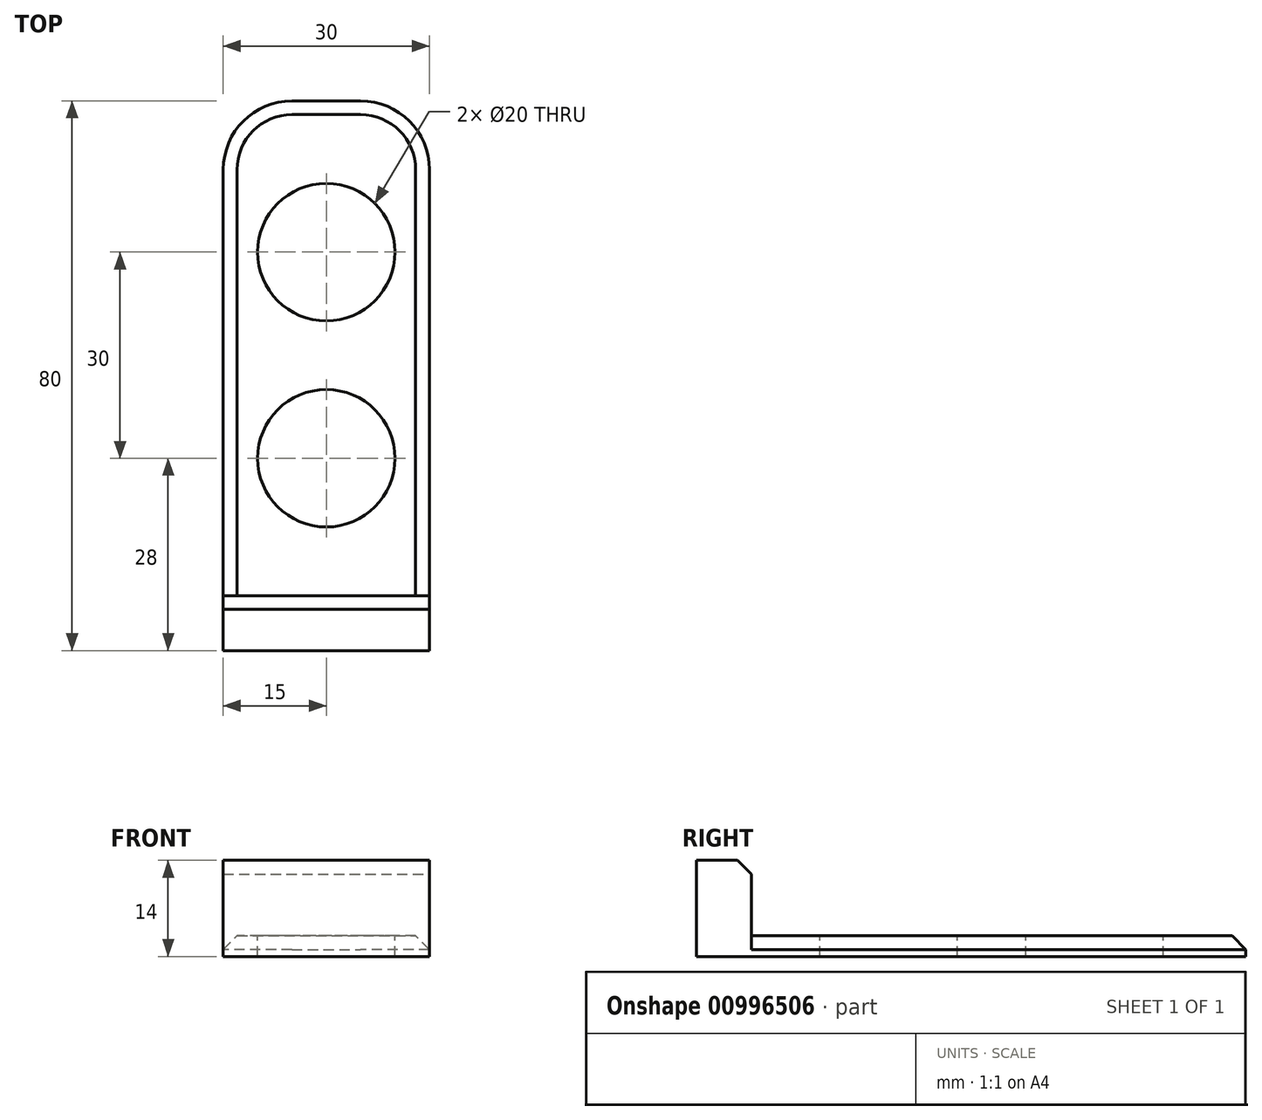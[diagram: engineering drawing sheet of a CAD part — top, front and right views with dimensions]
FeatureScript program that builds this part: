
annotation { "Feature Type Name" : "Feature", "Feature Type Description" : "" }
export const myFeature = defineFeature(function(context is Context, id is Id, definition is map)
    precondition{}
    {
        {
            var Q0;
            Q0=qCreatedBy(makeId("Top.planeOp"),FACE);
            var sketch = newSketch(context, id + "F0", { "sketchPlane" : qUnion([Q0])});
            skLineSegment(sketch, "E0.bottom", {"start": v(15, -40) * mm, "end": v(-15, -40) * mm});
            skLineSegment(sketch, "E0.top", {"start": v(15, 40) * mm, "end": v(-15, 40) * mm});
            skLineSegment(sketch, "E0.left", {"start": v(15, -40) * mm, "end": v(15, 40) * mm});
            skLineSegment(sketch, "E0.right", {"start": v(-15, -40) * mm, "end": v(-15, 40) * mm});
            skPoint(sketch, "E0.middle", {"position": v(0, 0) * mm});
            skSolve(sketch);
        }
        {
            var Q0;
            Q0=makeQuery(id+"F0.imprint","IMPRINT",FACE,{"disambiguationData":[TD([[makeQuery(id+"F0.imprint","IMPRINT",EDGE,{"derivedFrom":sQuery(id+"F0.wireOp",EDGE,"E0.bottom")}),-1.0]])]});
            extrude(context, id + "F1", {"entities" : qUnion([Q0]), "depth" : 3 * mm, "offsetDistance" : 25 * mm});
        }
        {
            var Q0;
            Q0=makeQuery(id+"F1.opExtrude","CAP_FACE",FACE,{"disambiguationData":[OSD([sQuery(id+"F0.wireOp",EDGE,"E0.bottom"),sQuery(id+"F0.wireOp",EDGE,"E0.top"),sQuery(id+"F0.wireOp",EDGE,"E0.left"),sQuery(id+"F0.wireOp",EDGE,"E0.right")])],"isStart":false});
            var sketch = newSketch(context, id + "F2", { "sketchPlane" : qUnion([Q0])});
            skLineSegment(sketch, "E1.bottom", {"start": v(-15, -40) * mm, "end": v(15, -40) * mm});
            skLineSegment(sketch, "E1.top", {"start": v(-15, -32) * mm, "end": v(15, -32) * mm});
            skLineSegment(sketch, "E1.left", {"start": v(-15, -40) * mm, "end": v(-15, -32) * mm});
            skLineSegment(sketch, "E1.right", {"start": v(15, -40) * mm, "end": v(15, -32) * mm});
            skSolve(sketch);
        }
        {
            var Q0;
            Q0=makeQuery(id+"F2.imprint","IMPRINT",FACE,{"disambiguationData":[TD([[makeQuery(id+"F2.imprint","IMPRINT",EDGE,{"derivedFrom":sQuery(id+"F2.wireOp",EDGE,"E1.bottom")}),-1.0]])]});
            extrude(context, id + "F3", {"entities" : qUnion([Q0]), "operationType" : NewBodyOperationType.ADD, "depth" : 11 * mm, "offsetDistance" : 25 * mm});
        }
        {
            var Q0;
            Q0=makeQuery(id+"F1.opExtrude","SWEPT_EDGE",EDGE,{"disambiguationData":[OSD([sQuery(id+"F0.wireOp",EDGE,"E0.top"),sQuery(id+"F0.wireOp",EDGE,"E0.right")])]});
            var Q1;
            Q1=makeQuery(id+"F1.opExtrude","SWEPT_EDGE",EDGE,{"disambiguationData":[OSD([sQuery(id+"F0.wireOp",EDGE,"E0.top"),sQuery(id+"F0.wireOp",EDGE,"E0.left")])]});
            fillet(context, id + "F4", {"entities" : qUnion([Q0, Q1]), "tangentPropagation" : true, "radius" : 10 * mm, "defaultsChanged" : true, "vertexSettings" : [], "allowEdgeOverflow" : false});
        }
        {
            var Q0;
            Q0=makeQuery(id+"F1.opExtrude","CAP_FACE",FACE,{"disambiguationData":[OSD([sQuery(id+"F0.wireOp",EDGE,"E0.bottom"),sQuery(id+"F0.wireOp",EDGE,"E0.top"),sQuery(id+"F0.wireOp",EDGE,"E0.left"),sQuery(id+"F0.wireOp",EDGE,"E0.right")])],"isStart":false});
            var sketch = newSketch(context, id + "F5", { "sketchPlane" : qUnion([Q0])});
            skCircle(sketch, "E2", {"center": v(0, 18) * mm, "radius": 10 * mm});
            skCircle(sketch, "E3", {"center": v(0, -12) * mm, "radius": 10 * mm});
            skSolve(sketch);
        }
        {
            var Q0;
            Q0=makeQuery(id+"F5.imprint","IMPRINT",FACE,{"disambiguationData":[TD([[makeQuery(id+"F5.imprint","IMPRINT",EDGE,{"derivedFrom":sQuery(id+"F5.wireOp",EDGE,"E2")}),1.0]])]});
            var Q1;
            Q1=makeQuery(id+"F5.imprint","IMPRINT",FACE,{"disambiguationData":[TD([[makeQuery(id+"F5.imprint","IMPRINT",EDGE,{"derivedFrom":sQuery(id+"F5.wireOp",EDGE,"E3")}),1.0]])]});
            extrude(context, id + "F6", {"entities" : qUnion([Q0, Q1]), "operationType" : NewBodyOperationType.REMOVE, "endBound" : BoundingType.THROUGH_ALL, "oppositeDirection" : true, "depth" : 25 * mm, "offsetDistance" : 25 * mm});
        }
        {
            var Q0;
            Q0=makeQuery(id+"F3.opExtrude","CAP_EDGE",EDGE,{"disambiguationData":[OSD([sQuery(id+"F2.wireOp",EDGE,"E1.top")])],"isStart":false});
            var Q1;
            Q1=makeQuery(id+"F1.opExtrude","CAP_EDGE",EDGE,{"disambiguationData":[OSD([sQuery(id+"F0.wireOp",EDGE,"E0.right")])],"isStart":false});
            var Q2;
            Q2=makeQuery(id+"F6.boolean.opBoolean","COPY",EDGE,{"derivedFrom":makeQuery(id+"F6.opExtrude","CAP_EDGE",EDGE,{"disambiguationData":[OSD([sQuery(id+"F5.wireOp",EDGE,"E2")])],"isStart":true})});
            var Q3;
            Q3=makeQuery(id+"F6.boolean.opBoolean","COPY",EDGE,{"derivedFrom":makeQuery(id+"F6.opExtrude","CAP_EDGE",EDGE,{"disambiguationData":[OSD([sQuery(id+"F5.wireOp",EDGE,"E3")])],"isStart":true})});
            chamfer(context, id + "F7", {"entities" : qUnion([Q0, Q1, Q2, Q3]), "width" : 2 * mm, "tangentPropagation" : true});
        }
    });
